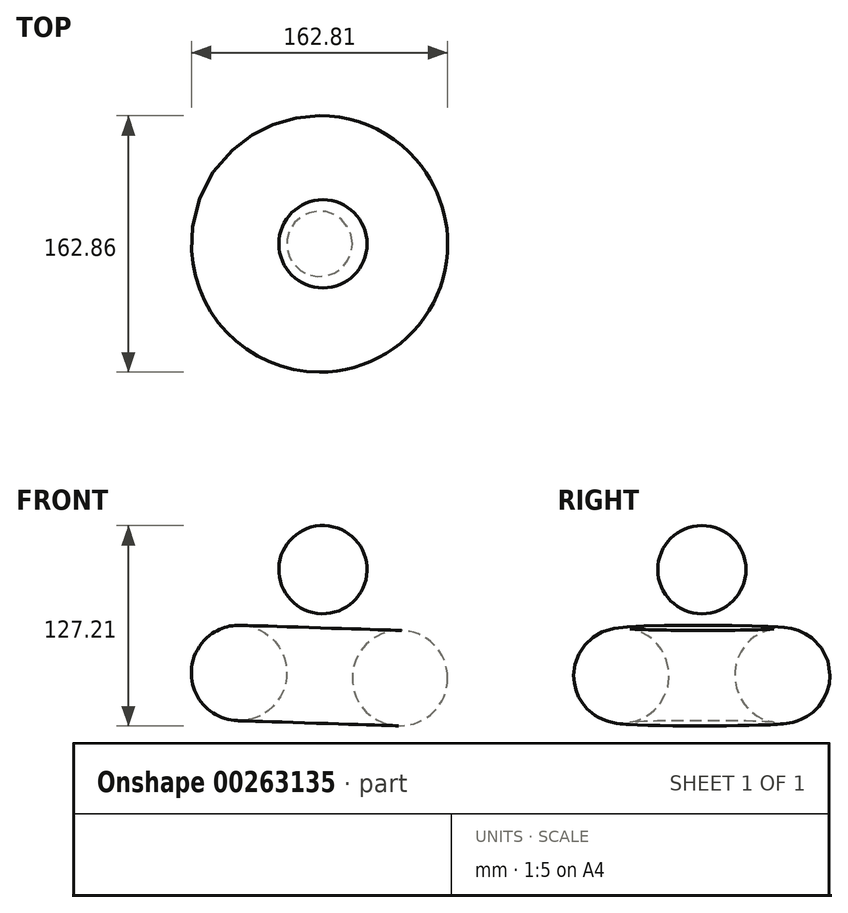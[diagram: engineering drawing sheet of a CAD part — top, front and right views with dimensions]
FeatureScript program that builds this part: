
annotation { "Feature Type Name" : "Feature", "Feature Type Description" : "" }
export const myFeature = defineFeature(function(context is Context, id is Id, definition is map)
    precondition{}
    {
        {
            var Q0;
            Q0=qCreatedBy(makeId("Front.planeOp"),FACE);
            var sketch = newSketch(context, id + "F0", { "sketchPlane" : qUnion([Q0])});
            skArc(sketch, "E0", {"start": v(-30.76, 104.27) * mm, "mid": v(-59.65, 77.19) * mm, "end": v(-32.57, 48.3) * mm});
            skCircle(sketch, "E1", {"center": v(17.27, 7.38) * mm, "radius": 30.3 * mm});
            skLineSegment(sketch, "E2", {"start": v(-29.98, 128.38) * mm, "end": v(-35.98, -57.38) * mm, "construction": true});
            skLineSegment(sketch, "E3", {"start": v(-32.57, 48.3) * mm, "end": v(-30.76, 104.27) * mm});
            skSolve(sketch);
        }
        {
            var Q0;
            Q0=makeQuery(id+"F0.imprint","IMPRINT",FACE,{"disambiguationData":[TD([[makeQuery(id+"F0.imprint","IMPRINT",EDGE,{"derivedFrom":sQuery(id+"F0.wireOp",EDGE,"E0")}),1.0]])]});
            var Q1;
            Q1=makeQuery(id+"F0.imprint","IMPRINT",FACE,{"disambiguationData":[TD([[makeQuery(id+"F0.imprint","IMPRINT",EDGE,{"derivedFrom":sQuery(id+"F0.wireOp",EDGE,"E1")}),1.0]])]});
            var Q2;
            Q2=sQuery(id+"F0.wireOp",EDGE,"E2");
            revolve(context, id + "F1", {"entities" : qUnion([Q0, Q1]), "axis" : qUnion([Q2]), "revolveType" : RevolveType.FULL});
        }
    });
